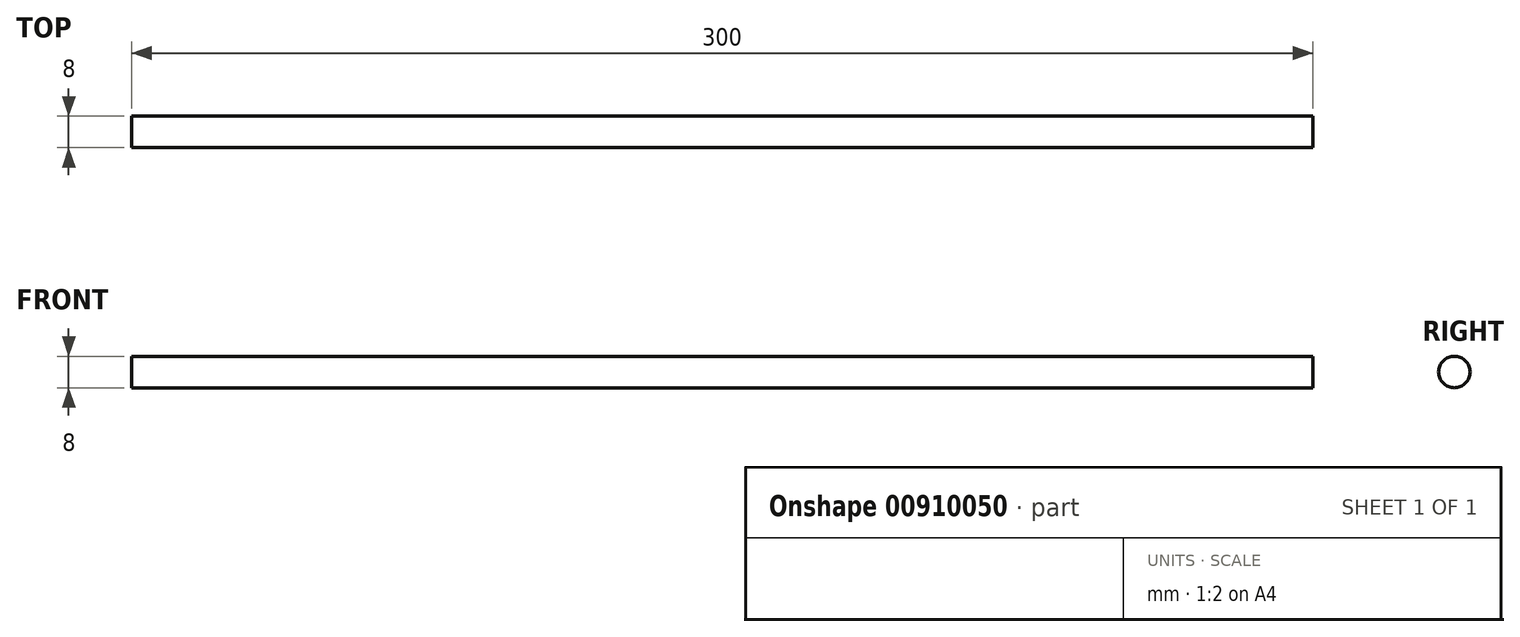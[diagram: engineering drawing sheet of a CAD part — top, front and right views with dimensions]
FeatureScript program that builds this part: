
annotation { "Feature Type Name" : "Feature", "Feature Type Description" : "" }
export const myFeature = defineFeature(function(context is Context, id is Id, definition is map)
    precondition{}
    {
        {
            var Q0;
            Q0=qCreatedBy(makeId("Right.planeOp"),FACE);
            var sketch = newSketch(context, id + "F0", { "sketchPlane" : qUnion([Q0])});
            skCircle(sketch, "E0", {"center": v(0, 0) * mm, "radius": 4 * mm});
            skSolve(sketch);
        }
        {
            var Q0;
            Q0=makeQuery(id+"F0.imprint","IMPRINT",FACE,{"disambiguationData":[TD([[makeQuery(id+"F0.imprint","IMPRINT",EDGE,{"derivedFrom":sQuery(id+"F0.wireOp",EDGE,"E0")}),1.0]])]});
            extrude(context, id + "F1", {"entities" : qUnion([Q0]), "depth" : 300 * mm, "offsetDistance" : 25 * mm});
        }
    });
